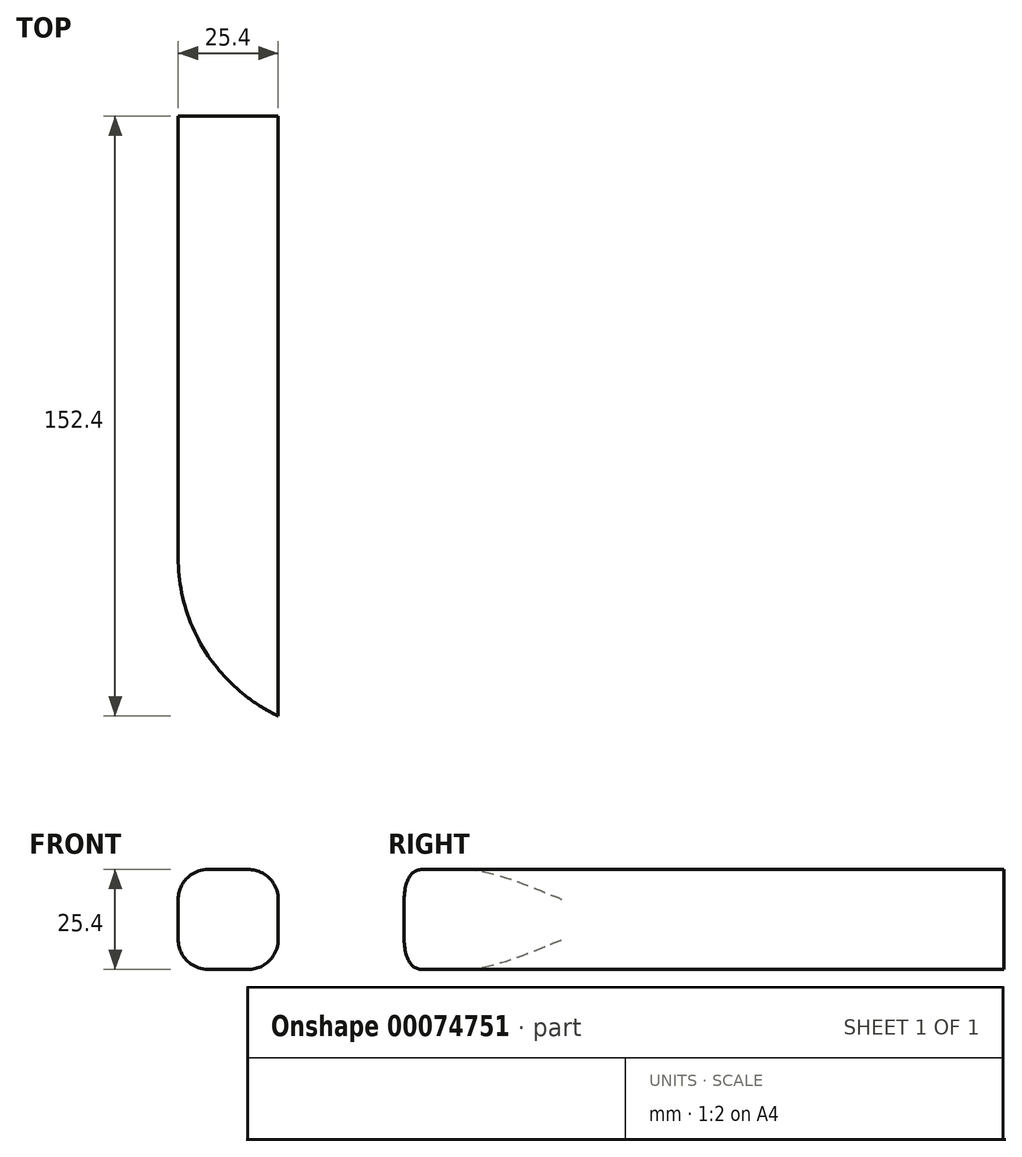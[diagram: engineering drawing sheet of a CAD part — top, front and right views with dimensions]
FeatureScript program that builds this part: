
annotation { "Feature Type Name" : "Feature", "Feature Type Description" : "" }
export const myFeature = defineFeature(function(context is Context, id is Id, definition is map)
    precondition{}
    {
        {
            var Q0;
            Q0=qCreatedBy(makeId("Front.planeOp"),FACE);
            var sketch = newSketch(context, id + "F0", { "sketchPlane" : qUnion([Q0])});
            skLineSegment(sketch, "E0.bottom", {"start": v(0, 0) * mm, "end": v(25.4, 0) * mm});
            skLineSegment(sketch, "E0.top", {"start": v(0, -25.4) * mm, "end": v(25.4, -25.4) * mm});
            skLineSegment(sketch, "E0.left", {"start": v(0, 0) * mm, "end": v(0, -25.4) * mm});
            skLineSegment(sketch, "E0.right", {"start": v(25.4, 0) * mm, "end": v(25.4, -25.4) * mm});
            skSolve(sketch);
        }
        {
            var Q0;
            Q0 = qSketchRegion(id + "F0", true);
            extrude(context, id + "F1", {"entities" : qUnion([Q0]), "oppositeDirection" : true, "depth" : 152.4 * mm});
        }
        {
            var Q0;
            Q0=makeQuery(id+"F1.opExtrude","SWEPT_EDGE",EDGE,{"disambiguationData":[OSD([sQuery(id+"F0.wireOp",EDGE,"E0.bottom"),sQuery(id+"F0.wireOp",EDGE,"E0.right")])]});
            fillet(context, id + "F2", {"entities" : qUnion([Q0]), "radius" : 7.62 * mm, "tangentPropagation" : true, "allowEdgeOverflow" : false});
        }
        {
            var Q0;
            Q0=makeQuery(id+"F1.opExtrude","SWEPT_EDGE",EDGE,{"disambiguationData":[OSD([sQuery(id+"F0.wireOp",EDGE,"E0.bottom"),sQuery(id+"F0.wireOp",EDGE,"E0.left")])]});
            fillet(context, id + "F3", {"entities" : qUnion([Q0]), "radius" : 7.62 * mm, "tangentPropagation" : true, "allowEdgeOverflow" : false});
        }
        {
            var Q0;
            Q0=makeQuery(id+"F1.opExtrude","SWEPT_EDGE",EDGE,{"disambiguationData":[OSD([sQuery(id+"F0.wireOp",EDGE,"E0.top"),sQuery(id+"F0.wireOp",EDGE,"E0.right")])]});
            fillet(context, id + "F4", {"entities" : qUnion([Q0]), "radius" : 7.62 * mm, "tangentPropagation" : true, "allowEdgeOverflow" : false});
        }
        {
            var Q0;
            Q0=makeQuery(id+"F1.opExtrude","SWEPT_EDGE",EDGE,{"disambiguationData":[OSD([sQuery(id+"F0.wireOp",EDGE,"E0.top"),sQuery(id+"F0.wireOp",EDGE,"E0.left")])]});
            fillet(context, id + "F5", {"entities" : qUnion([Q0]), "radius" : 7.62 * mm, "tangentPropagation" : true, "allowEdgeOverflow" : false});
        }
        {
            var Q0;
            Q0=makeQuery(id+"F1.opExtrude","CAP_EDGE",EDGE,{"disambiguationData":[OSD([sQuery(id+"F0.wireOp",EDGE,"E0.left")])],"isStart":true});
            fillet(context, id + "F6", {"entities" : qUnion([Q0]), "radius" : 44.45 * mm, "allowEdgeOverflow" : false});
        }
    });
